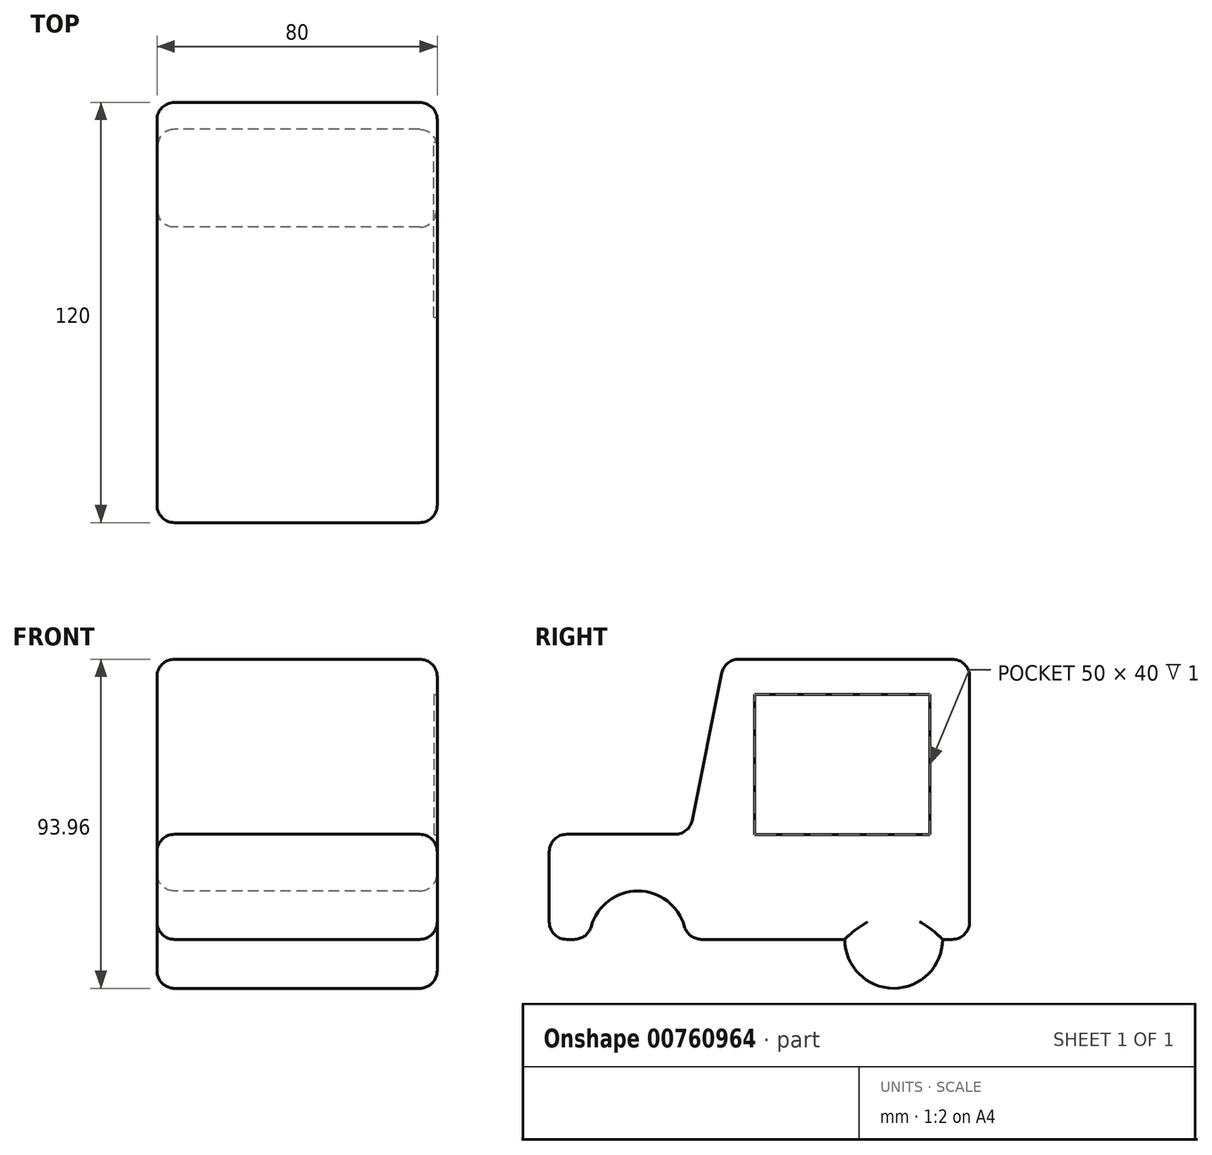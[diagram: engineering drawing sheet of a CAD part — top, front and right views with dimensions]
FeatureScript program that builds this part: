
annotation { "Feature Type Name" : "Feature", "Feature Type Description" : "" }
export const myFeature = defineFeature(function(context is Context, id is Id, definition is map)
    precondition{}
    {
        {
            var Q0;
            Q0=qCreatedBy(makeId("Right.planeOp"),FACE);
            var sketch = newSketch(context, id + "F0", { "sketchPlane" : qUnion([Q0])});
            skLineSegment(sketch, "E0", {"start": v(-79.77, 12.08) * mm, "end": v(40.23, 12.08) * mm});
            skLineSegment(sketch, "E1", {"start": v(40.23, 12.08) * mm, "end": v(40.23, 92.08) * mm});
            skLineSegment(sketch, "E2", {"start": v(40.23, 92.08) * mm, "end": v(-29.77, 92.08) * mm});
            skLineSegment(sketch, "E3", {"start": v(-79.77, 12.08) * mm, "end": v(-79.77, 42.08) * mm});
            skLineSegment(sketch, "E4", {"start": v(-79.77, 42.08) * mm, "end": v(-39.77, 42.08) * mm});
            skLineSegment(sketch, "E5", {"start": v(-39.77, 42.08) * mm, "end": v(-29.77, 92.08) * mm});
            skCircle(sketch, "E6", {"center": v(-54.48, 12.08) * mm, "radius": 13.82 * mm});
            skCircle(sketch, "E7", {"center": v(18.57, 12.08) * mm, "radius": 13.96 * mm});
            skSolve(sketch);
        }
        {
            var Q0;
            {var subQ0=sQuery(id+"F0.wireOp",EDGE,"E1");Q0=makeQuery(id+"F0.imprint","IMPRINT",FACE,{"disambiguationData":[TD([[makeQuery(id+"F0.imprint","IMPRINT",EDGE,{"derivedFrom":subQ0}),1.0]])]});}
            var Q1;
            {var subQ0=sQuery(id+"F0.wireOp",EDGE,"E6");var subQ1=sQuery(id+"F0.wireOp",EDGE,"E0");var subQ2=makeQuery(id+"F0.imprint","INTERSECT",VERTEX,{"disambiguationData":[OD(0.0)],"derivedFrom":[subQ1,subQ0]});Q1=makeQuery(id+"F0.imprint","IMPRINT",FACE,{"disambiguationData":[TD([[makeQuery(id+"F0.imprint","IMPRINT",EDGE,{"disambiguationData":[TD([[subQ2,-1.0]])],"derivedFrom":subQ1}),1.0]])]});}
            var Q2;
            {var subQ0=sQuery(id+"F0.wireOp",EDGE,"E6");var subQ1=sQuery(id+"F0.wireOp",EDGE,"E0");var subQ2=makeQuery(id+"F0.imprint","INTERSECT",VERTEX,{"disambiguationData":[OD(0.0)],"derivedFrom":[subQ1,subQ0]});Q2=makeQuery(id+"F0.imprint","IMPRINT",FACE,{"disambiguationData":[TD([[makeQuery(id+"F0.imprint","IMPRINT",EDGE,{"disambiguationData":[TD([[subQ2,-1.0]])],"derivedFrom":subQ1}),-1.0]])]});}
            var Q3;
            {var subQ0=sQuery(id+"F0.wireOp",EDGE,"E7");var subQ1=sQuery(id+"F0.wireOp",EDGE,"E0");var subQ2=makeQuery(id+"F0.imprint","INTERSECT",VERTEX,{"disambiguationData":[OD(0.0)],"derivedFrom":[subQ1,subQ0]});Q3=makeQuery(id+"F0.imprint","IMPRINT",FACE,{"disambiguationData":[TD([[makeQuery(id+"F0.imprint","IMPRINT",EDGE,{"disambiguationData":[TD([[subQ2,-1.0]])],"derivedFrom":subQ1}),1.0]])]});}
            var Q4;
            {var subQ0=sQuery(id+"F0.wireOp",EDGE,"E7");var subQ1=sQuery(id+"F0.wireOp",EDGE,"E0");var subQ2=makeQuery(id+"F0.imprint","INTERSECT",VERTEX,{"disambiguationData":[OD(0.0)],"derivedFrom":[subQ1,subQ0]});Q4=makeQuery(id+"F0.imprint","IMPRINT",FACE,{"disambiguationData":[TD([[makeQuery(id+"F0.imprint","IMPRINT",EDGE,{"disambiguationData":[TD([[subQ2,-1.0]])],"derivedFrom":subQ1}),-1.0]])]});}
            extrude(context, id + "F1", {"entities" : qUnion([Q0, Q1, Q2, Q3, Q4]), "endBound" : BoundingType.SYMMETRIC, "depth" : 80 * mm, "offsetDistance" : 25 * mm});
        }
        {
            var Q0;
            Q0=makeQuery(id+"F1.opExtrude","SWEPT_FACE",FACE,{"disambiguationData":[OSD([sQuery(id+"F0.wireOp",EDGE,"E5")])]});
            var Q1;
            Q1=makeQuery(id+"F1.opExtrude","SWEPT_FACE",FACE,{"disambiguationData":[OSD([sQuery(id+"F0.wireOp",EDGE,"E3")])]});
            var Q2;
            Q2=makeQuery(id+"F1.opExtrude","SWEPT_FACE",FACE,{"disambiguationData":[OSD([sQuery(id+"F0.wireOp",EDGE,"E6")])]});
            var Q3;
            Q3=makeQuery(id+"F1.opExtrude","CAP_FACE",FACE,{"disambiguationData":[OSD([sQuery(id+"F0.wireOp",EDGE,"E0"),sQuery(id+"F0.wireOp",EDGE,"E1"),sQuery(id+"F0.wireOp",EDGE,"E2"),sQuery(id+"F0.wireOp",EDGE,"E3"),sQuery(id+"F0.wireOp",EDGE,"E4"),sQuery(id+"F0.wireOp",EDGE,"E5"),sQuery(id+"F0.wireOp",EDGE,"E6"),sQuery(id+"F0.wireOp",EDGE,"E7")])],"isStart":true});
            var Q4;
            Q4=makeQuery(id+"F1.opExtrude","SWEPT_FACE",FACE,{"disambiguationData":[OSD([sQuery(id+"F0.wireOp",EDGE,"E1")])]});
            var Q5;
            Q5=makeQuery(id+"F1.opExtrude","CAP_FACE",FACE,{"disambiguationData":[OSD([sQuery(id+"F0.wireOp",EDGE,"E0"),sQuery(id+"F0.wireOp",EDGE,"E1"),sQuery(id+"F0.wireOp",EDGE,"E2"),sQuery(id+"F0.wireOp",EDGE,"E3"),sQuery(id+"F0.wireOp",EDGE,"E4"),sQuery(id+"F0.wireOp",EDGE,"E5"),sQuery(id+"F0.wireOp",EDGE,"E6"),sQuery(id+"F0.wireOp",EDGE,"E7")])],"isStart":false});
            fillet(context, id + "F2", {"entities" : qUnion([Q0, Q1, Q2, Q3, Q4, Q5]), "radius" : 5 * mm, "tangentPropagation" : true, "allowEdgeOverflow" : false});
        }
        {
            var Q0;
            Q0=makeQuery(id+"F1.opExtrude","CAP_FACE",FACE,{"disambiguationData":[OSD([sQuery(id+"F0.wireOp",EDGE,"E0"),sQuery(id+"F0.wireOp",EDGE,"E1"),sQuery(id+"F0.wireOp",EDGE,"E2"),sQuery(id+"F0.wireOp",EDGE,"E3"),sQuery(id+"F0.wireOp",EDGE,"E4"),sQuery(id+"F0.wireOp",EDGE,"E5"),sQuery(id+"F0.wireOp",EDGE,"E6"),sQuery(id+"F0.wireOp",EDGE,"E7")])],"isStart":false});
            var sketch = newSketch(context, id + "F3", { "sketchPlane" : qUnion([Q0])});
            skLineSegment(sketch, "E8.bottom", {"start": v(-21.12, 81.98) * mm, "end": v(28.88, 81.98) * mm});
            skLineSegment(sketch, "E8.top", {"start": v(-21.12, 41.98) * mm, "end": v(28.88, 41.98) * mm});
            skLineSegment(sketch, "E8.left", {"start": v(-21.12, 81.98) * mm, "end": v(-21.12, 41.98) * mm});
            skLineSegment(sketch, "E8.right", {"start": v(28.88, 81.98) * mm, "end": v(28.88, 41.98) * mm});
            skSolve(sketch);
        }
        {
            var Q0;
            Q0 = qSketchRegion(id + "F3", true);
            extrude(context, id + "F4", {"entities" : qUnion([Q0]), "operationType" : NewBodyOperationType.REMOVE, "endBound" : BoundingType.SYMMETRIC, "oppositeDirection" : true, "depth" : 2 * mm, "offsetDistance" : 25 * mm});
        }
    });
